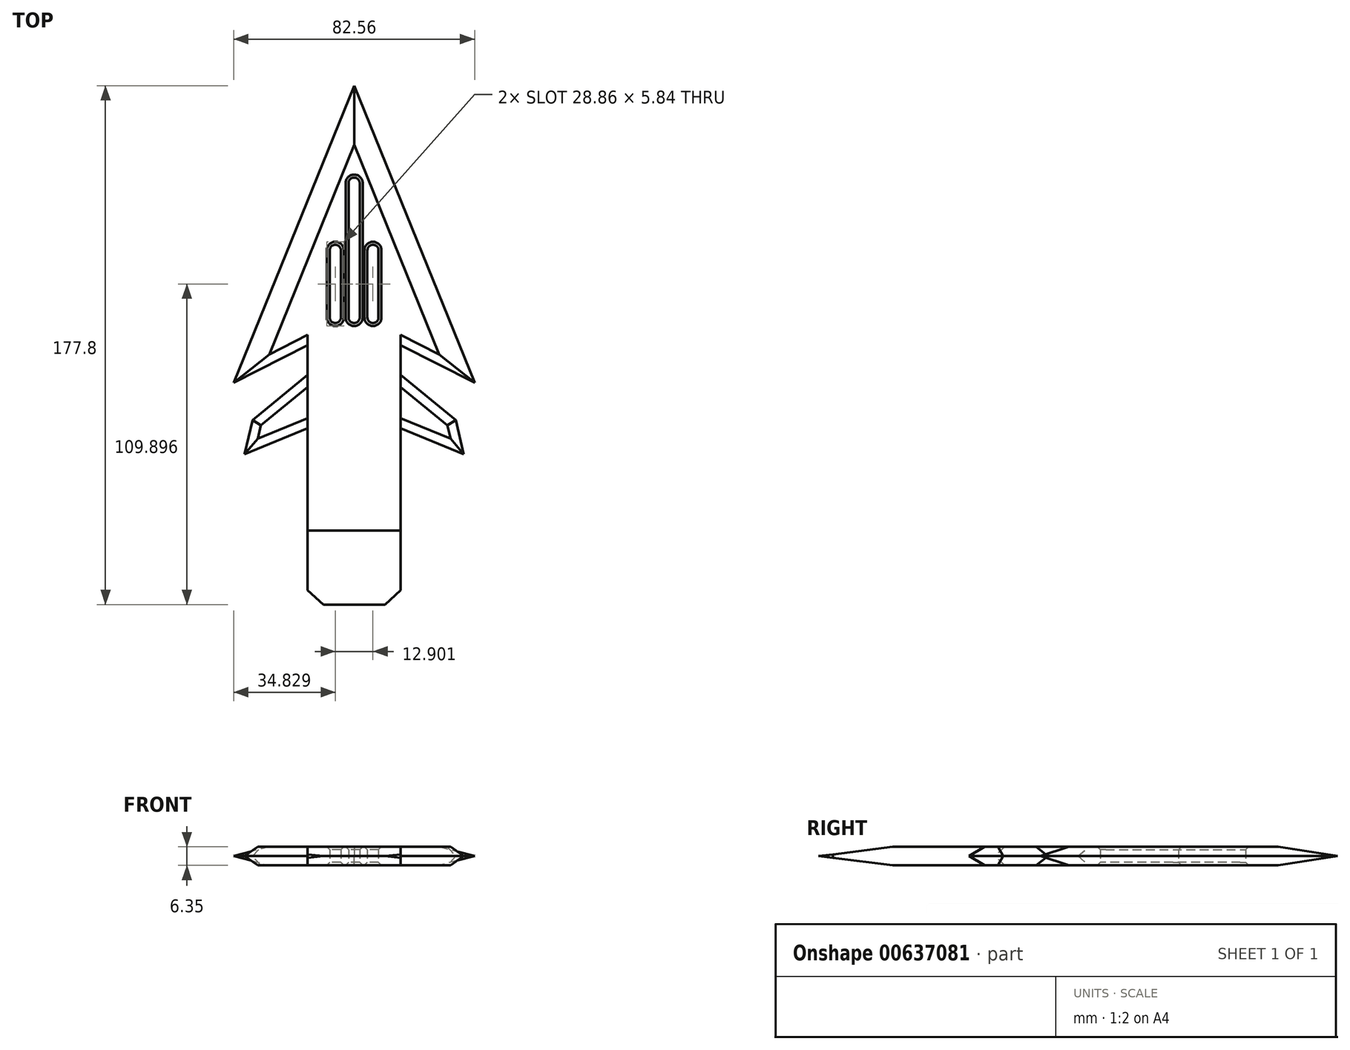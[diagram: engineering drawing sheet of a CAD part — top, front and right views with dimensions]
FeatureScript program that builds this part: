
annotation { "Feature Type Name" : "Feature", "Feature Type Description" : "" }
export const myFeature = defineFeature(function(context is Context, id is Id, definition is map)
    precondition{}
    {
        {
            var Q0;
            Q0=qCreatedBy(makeId("Top.planeOp"),FACE);
            var sketch = newSketch(context, id + "F0", { "sketchPlane" : qUnion([Q0])});
            skPoint(sketch, "E0.middle", {"position": v(0, 0) * mm});
            skLineSegment(sketch, "E1", {"start": v(0, 88.9) * mm, "end": v(41.28, -12.87) * mm});
            skLineSegment(sketch, "E2.MirrorCS", {"start": v(0, 88.9) * mm, "end": v(-41.28, -12.87) * mm});
            skLineSegment(sketch, "E3", {"start": v(15.9, -10.25) * mm, "end": v(34.78, -25.68) * mm});
            skLineSegment(sketch, "E4", {"start": v(34.78, -25.68) * mm, "end": v(37.57, -37.31) * mm});
            skLineSegment(sketch, "E5", {"start": v(37.57, -37.31) * mm, "end": v(15.9, -28.53) * mm});
            skLineSegment(sketch, "E6.MirrorCS", {"start": v(-15.9, -10.25) * mm, "end": v(-34.78, -25.68) * mm});
            skLineSegment(sketch, "E7.MirrorCS", {"start": v(-34.78, -25.68) * mm, "end": v(-37.57, -37.31) * mm});
            skLineSegment(sketch, "E8.MirrorCS", {"start": v(-37.57, -37.31) * mm, "end": v(-15.9, -28.53) * mm});
            skLineSegment(sketch, "E9", {"start": v(0, 55.53) * mm, "end": v(0, 9.49) * mm});
            skLineSegment(sketch, "E10", {"start": v(6.45, 32.5) * mm, "end": v(6.45, 9.49) * mm});
            skPoint(sketch, "E10.startSnap0", {"position": v(0, 32.5) * mm});
            skLineSegment(sketch, "E11.MirrorCS", {"start": v(-6.45, 32.5) * mm, "end": v(-6.45, 9.49) * mm});
            skArc(sketch, "E12.0.startCap", {"start": v(-1.9, 55.53) * mm, "mid": v(0, 57.43) * mm, "end": v(1.9, 55.53) * mm});
            skArc(sketch, "E12.0.endCap", {"start": v(1.9, 9.49) * mm, "mid": v(0, 7.58) * mm, "end": v(-1.9, 9.49) * mm});
            skLineSegment(sketch, "E12.0.left", {"start": v(1.9, 55.53) * mm, "end": v(1.9, 9.49) * mm});
            skLineSegment(sketch, "E12.0.right", {"start": v(-1.9, 55.53) * mm, "end": v(-1.9, 9.49) * mm});
            skArc(sketch, "E12.1.startCap", {"start": v(4.55, 32.5) * mm, "mid": v(6.45, 34.41) * mm, "end": v(8.36, 32.5) * mm});
            skArc(sketch, "E12.1.endCap", {"start": v(8.36, 9.49) * mm, "mid": v(6.45, 7.58) * mm, "end": v(4.55, 9.49) * mm});
            skLineSegment(sketch, "E12.1.left", {"start": v(8.36, 32.5) * mm, "end": v(8.36, 9.49) * mm});
            skLineSegment(sketch, "E12.1.right", {"start": v(4.55, 32.5) * mm, "end": v(4.55, 9.49) * mm});
            skArc(sketch, "E12.2.startCap", {"start": v(-8.36, 32.5) * mm, "mid": v(-6.45, 34.41) * mm, "end": v(-4.55, 32.5) * mm});
            skArc(sketch, "E12.2.endCap", {"start": v(-4.55, 9.49) * mm, "mid": v(-6.45, 7.58) * mm, "end": v(-8.36, 9.49) * mm});
            skLineSegment(sketch, "E12.2.left", {"start": v(-4.55, 32.5) * mm, "end": v(-4.55, 9.49) * mm});
            skLineSegment(sketch, "E12.2.right", {"start": v(-8.36, 32.5) * mm, "end": v(-8.36, 9.49) * mm});
            skLineSegment(sketch, "E13", {"start": v(-15.9, -83.97) * mm, "end": v(-10.53, -88.9) * mm});
            skLineSegment(sketch, "E14.MirrorCS", {"start": v(15.9, -83.97) * mm, "end": v(10.53, -88.9) * mm});
            skLineSegment(sketch, "E15", {"start": v(-15.9, 0) * mm, "end": v(-15.9, -83.97) * mm});
            skLineSegment(sketch, "E16.MirrorCS", {"start": v(15.9, 0) * mm, "end": v(15.9, -83.97) * mm});
            skLineSegment(sketch, "E17", {"start": v(-10.53, -88.9) * mm, "end": v(10.53, -88.9) * mm});
            skLineSegment(sketch, "E18", {"start": v(-15.9, 0) * mm, "end": v(-41.28, -12.87) * mm});
            skLineSegment(sketch, "E19", {"start": v(41.28, -12.87) * mm, "end": v(15.9, 0) * mm});
            skSolve(sketch);
        }
        {
            var Q0;
            Q0=makeQuery(id+"F0.imprint","IMPRINT",FACE,{"disambiguationData":[TD([[makeQuery(id+"F0.imprint","IMPRINT",EDGE,{"derivedFrom":sQuery(id+"F0.wireOp",EDGE,"E1")}),-1.0]])]});
            extrude(context, id + "F1", {"entities" : qUnion([Q0]), "depth" : 6.35 * mm, "offsetDistance" : 25.4 * mm});
        }
        {
            var Q0;
            {var subQ0=sQuery(id+"F0.wireOp",EDGE,"E6.MirrorCS");Q0=makeQuery(id+"F0.imprint","IMPRINT",FACE,{"disambiguationData":[TD([[makeQuery(id+"F0.imprint","IMPRINT",EDGE,{"derivedFrom":subQ0}),1.0]])]});}
            extrude(context, id + "F2", {"entities" : qUnion([Q0]), "depth" : 6.35 * mm, "offsetDistance" : 25.4 * mm});
        }
        {
            var Q0;
            {var subQ0=sQuery(id+"F0.wireOp",EDGE,"E3");Q0=makeQuery(id+"F0.imprint","IMPRINT",FACE,{"disambiguationData":[TD([[makeQuery(id+"F0.imprint","IMPRINT",EDGE,{"derivedFrom":subQ0}),-1.0]])]});}
            extrude(context, id + "F3", {"entities" : qUnion([Q0]), "depth" : 6.35 * mm, "offsetDistance" : 25.4 * mm});
        }
        {
            var Q0;
            Q0=makeQuery(id+"F1.opExtrude","CAP_EDGE",EDGE,{"disambiguationData":[OSD([sQuery(id+"F0.wireOp",EDGE,"E1")])],"isStart":false});
            var Q1;
            Q1=makeQuery(id+"F1.opExtrude","CAP_EDGE",EDGE,{"disambiguationData":[OSD([sQuery(id+"F0.wireOp",EDGE,"E2.MirrorCS")])],"isStart":false});
            var Q2;
            Q2=makeQuery(id+"F1.opExtrude","CAP_EDGE",EDGE,{"disambiguationData":[OSD([sQuery(id+"F0.wireOp",EDGE,"E2.MirrorCS")])],"isStart":true});
            var Q3;
            Q3=makeQuery(id+"F1.opExtrude","CAP_EDGE",EDGE,{"disambiguationData":[OSD([sQuery(id+"F0.wireOp",EDGE,"E1")])],"isStart":true});
            chamfer(context, id + "F4", {"entities" : qUnion([Q0, Q1, Q2, Q3]), "chamferType" : ChamferType.TWO_OFFSETS, "width1" : 3.17 * mm, "oppositeDirection" : false, "width2" : 7.62 * mm, "tangentPropagation" : true});
        }
        {
            var Q0;
            Q0=makeQuery(id+"F1.opExtrude","CAP_EDGE",EDGE,{"disambiguationData":[OSD([sQuery(id+"F0.wireOp",EDGE,"E19")])],"isStart":false});
            var Q1;
            Q1=makeQuery(id+"F1.opExtrude","CAP_EDGE",EDGE,{"disambiguationData":[OSD([sQuery(id+"F0.wireOp",EDGE,"E19")])],"isStart":true});
            var Q2;
            Q2=makeQuery(id+"F1.opExtrude","CAP_EDGE",EDGE,{"disambiguationData":[OSD([sQuery(id+"F0.wireOp",EDGE,"E18")])],"isStart":false});
            var Q3;
            Q3=makeQuery(id+"F1.opExtrude","CAP_EDGE",EDGE,{"disambiguationData":[OSD([sQuery(id+"F0.wireOp",EDGE,"E18")])],"isStart":true});
            chamfer(context, id + "F5", {"entities" : qUnion([Q0, Q1, Q2, Q3]), "chamferType" : ChamferType.TWO_OFFSETS, "width1" : 3.17 * mm, "oppositeDirection" : false, "width2" : 3.17 * mm, "tangentPropagation" : true});
        }
        {
            var Q0;
            Q0=makeQuery(id+"F2.opExtrude","CAP_EDGE",EDGE,{"disambiguationData":[OSD([sQuery(id+"F0.wireOp",EDGE,"E6.MirrorCS")])],"isStart":false});
            var Q1;
            Q1=makeQuery(id+"F2.opExtrude","CAP_EDGE",EDGE,{"disambiguationData":[OSD([sQuery(id+"F0.wireOp",EDGE,"E6.MirrorCS")])],"isStart":true});
            var Q2;
            Q2=makeQuery(id+"F2.opExtrude","CAP_EDGE",EDGE,{"disambiguationData":[OSD([sQuery(id+"F0.wireOp",EDGE,"E7.MirrorCS")])],"isStart":false});
            var Q3;
            Q3=makeQuery(id+"F2.opExtrude","CAP_EDGE",EDGE,{"disambiguationData":[OSD([sQuery(id+"F0.wireOp",EDGE,"E7.MirrorCS")])],"isStart":true});
            var Q4;
            Q4=makeQuery(id+"F2.opExtrude","CAP_EDGE",EDGE,{"disambiguationData":[OSD([sQuery(id+"F0.wireOp",EDGE,"E8.MirrorCS")])],"isStart":true});
            var Q5;
            Q5=makeQuery(id+"F2.opExtrude","CAP_EDGE",EDGE,{"disambiguationData":[OSD([sQuery(id+"F0.wireOp",EDGE,"E8.MirrorCS")])],"isStart":false});
            var Q6;
            Q6=makeQuery(id+"F3.opExtrude","CAP_EDGE",EDGE,{"disambiguationData":[OSD([sQuery(id+"F0.wireOp",EDGE,"E3")])],"isStart":false});
            var Q7;
            Q7=makeQuery(id+"F3.opExtrude","CAP_EDGE",EDGE,{"disambiguationData":[OSD([sQuery(id+"F0.wireOp",EDGE,"E3")])],"isStart":true});
            var Q8;
            Q8=makeQuery(id+"F3.opExtrude","CAP_EDGE",EDGE,{"disambiguationData":[OSD([sQuery(id+"F0.wireOp",EDGE,"E4")])],"isStart":true});
            var Q9;
            Q9=makeQuery(id+"F3.opExtrude","CAP_EDGE",EDGE,{"disambiguationData":[OSD([sQuery(id+"F0.wireOp",EDGE,"E4")])],"isStart":false});
            var Q10;
            Q10=makeQuery(id+"F3.opExtrude","CAP_EDGE",EDGE,{"disambiguationData":[OSD([sQuery(id+"F0.wireOp",EDGE,"E5")])],"isStart":false});
            var Q11;
            Q11=makeQuery(id+"F3.opExtrude","CAP_EDGE",EDGE,{"disambiguationData":[OSD([sQuery(id+"F0.wireOp",EDGE,"E5")])],"isStart":true});
            chamfer(context, id + "F6", {"entities" : qUnion([Q0, Q1, Q2, Q3, Q4, Q5, Q6, Q7, Q8, Q9, Q10, Q11]), "chamferType" : ChamferType.TWO_OFFSETS, "width1" : 3.17 * mm, "oppositeDirection" : false, "width2" : 3.17 * mm, "tangentPropagation" : true});
        }
        {
            var Q0;
            Q0=makeQuery(id+"F1.opExtrude","CAP_EDGE",EDGE,{"disambiguationData":[OSD([sQuery(id+"F0.wireOp",EDGE,"E12.2.right")])],"isStart":false});
            var Q1;
            Q1=makeQuery(id+"F1.opExtrude","CAP_EDGE",EDGE,{"disambiguationData":[OSD([sQuery(id+"F0.wireOp",EDGE,"E12.2.endCap")])],"isStart":false});
            var Q2;
            Q2=makeQuery(id+"F1.opExtrude","CAP_EDGE",EDGE,{"disambiguationData":[OSD([sQuery(id+"F0.wireOp",EDGE,"E12.2.left")])],"isStart":false});
            var Q3;
            Q3=makeQuery(id+"F1.opExtrude","CAP_EDGE",EDGE,{"disambiguationData":[OSD([sQuery(id+"F0.wireOp",EDGE,"E12.2.startCap")])],"isStart":false});
            var Q4;
            Q4=makeQuery(id+"F1.opExtrude","CAP_EDGE",EDGE,{"disambiguationData":[OSD([sQuery(id+"F0.wireOp",EDGE,"E12.0.right")])],"isStart":false});
            var Q5;
            Q5=makeQuery(id+"F1.opExtrude","CAP_EDGE",EDGE,{"disambiguationData":[OSD([sQuery(id+"F0.wireOp",EDGE,"E12.0.endCap")])],"isStart":false});
            var Q6;
            Q6=makeQuery(id+"F1.opExtrude","CAP_EDGE",EDGE,{"disambiguationData":[OSD([sQuery(id+"F0.wireOp",EDGE,"E12.0.left")])],"isStart":false});
            var Q7;
            Q7=makeQuery(id+"F1.opExtrude","CAP_EDGE",EDGE,{"disambiguationData":[OSD([sQuery(id+"F0.wireOp",EDGE,"E12.0.startCap")])],"isStart":false});
            var Q8;
            Q8=makeQuery(id+"F1.opExtrude","CAP_EDGE",EDGE,{"disambiguationData":[OSD([sQuery(id+"F0.wireOp",EDGE,"E12.1.left")])],"isStart":false});
            var Q9;
            Q9=makeQuery(id+"F1.opExtrude","CAP_EDGE",EDGE,{"disambiguationData":[OSD([sQuery(id+"F0.wireOp",EDGE,"E12.1.startCap")])],"isStart":false});
            var Q10;
            Q10=makeQuery(id+"F1.opExtrude","CAP_EDGE",EDGE,{"disambiguationData":[OSD([sQuery(id+"F0.wireOp",EDGE,"E12.1.right")])],"isStart":false});
            var Q11;
            Q11=makeQuery(id+"F1.opExtrude","CAP_EDGE",EDGE,{"disambiguationData":[OSD([sQuery(id+"F0.wireOp",EDGE,"E12.1.endCap")])],"isStart":false});
            var Q12;
            Q12=makeQuery(id+"F1.opExtrude","CAP_EDGE",EDGE,{"disambiguationData":[OSD([sQuery(id+"F0.wireOp",EDGE,"E12.2.endCap")])],"isStart":true});
            var Q13;
            Q13=makeQuery(id+"F1.opExtrude","CAP_EDGE",EDGE,{"disambiguationData":[OSD([sQuery(id+"F0.wireOp",EDGE,"E12.0.endCap")])],"isStart":true});
            var Q14;
            Q14=makeQuery(id+"F1.opExtrude","CAP_EDGE",EDGE,{"disambiguationData":[OSD([sQuery(id+"F0.wireOp",EDGE,"E12.1.endCap")])],"isStart":true});
            var Q15;
            Q15=makeQuery(id+"F1.opExtrude","CAP_EDGE",EDGE,{"disambiguationData":[OSD([sQuery(id+"F0.wireOp",EDGE,"E12.1.right")])],"isStart":true});
            var Q16;
            Q16=makeQuery(id+"F1.opExtrude","CAP_EDGE",EDGE,{"disambiguationData":[OSD([sQuery(id+"F0.wireOp",EDGE,"E12.1.left")])],"isStart":true});
            var Q17;
            Q17=makeQuery(id+"F1.opExtrude","CAP_EDGE",EDGE,{"disambiguationData":[OSD([sQuery(id+"F0.wireOp",EDGE,"E12.0.right")])],"isStart":true});
            var Q18;
            Q18=makeQuery(id+"F1.opExtrude","CAP_EDGE",EDGE,{"disambiguationData":[OSD([sQuery(id+"F0.wireOp",EDGE,"E12.0.left")])],"isStart":true});
            var Q19;
            Q19=makeQuery(id+"F1.opExtrude","CAP_EDGE",EDGE,{"disambiguationData":[OSD([sQuery(id+"F0.wireOp",EDGE,"E12.2.left")])],"isStart":true});
            var Q20;
            Q20=makeQuery(id+"F1.opExtrude","CAP_EDGE",EDGE,{"disambiguationData":[OSD([sQuery(id+"F0.wireOp",EDGE,"E12.2.right")])],"isStart":true});
            var Q21;
            Q21=makeQuery(id+"F1.opExtrude","CAP_EDGE",EDGE,{"disambiguationData":[OSD([sQuery(id+"F0.wireOp",EDGE,"E12.1.startCap")])],"isStart":true});
            var Q22;
            Q22=makeQuery(id+"F1.opExtrude","CAP_EDGE",EDGE,{"disambiguationData":[OSD([sQuery(id+"F0.wireOp",EDGE,"E12.2.startCap")])],"isStart":true});
            var Q23;
            Q23=makeQuery(id+"F1.opExtrude","CAP_EDGE",EDGE,{"disambiguationData":[OSD([sQuery(id+"F0.wireOp",EDGE,"E12.0.startCap")])],"isStart":true});
            chamfer(context, id + "F7", {"entities" : qUnion([Q0, Q1, Q2, Q3, Q4, Q5, Q6, Q7, Q8, Q9, Q10, Q11, Q12, Q13, Q14, Q15, Q16, Q17, Q18, Q19, Q20, Q21, Q22, Q23]), "width" : 1.02 * mm, "tangentPropagation" : true});
        }
        {
            var Q0;
            Q0=makeQuery(id+"F1.opExtrude","CAP_EDGE",EDGE,{"disambiguationData":[OSD([sQuery(id+"F0.wireOp",EDGE,"E17")])],"isStart":false});
            var Q1;
            Q1=makeQuery(id+"F1.opExtrude","CAP_EDGE",EDGE,{"disambiguationData":[OSD([sQuery(id+"F0.wireOp",EDGE,"E17")])],"isStart":true});
            chamfer(context, id + "F8", {"entities" : qUnion([Q0, Q1]), "chamferType" : ChamferType.TWO_OFFSETS, "width1" : 25.4 * mm, "oppositeDirection" : false, "width2" : 3.17 * mm, "tangentPropagation" : true});
        }
    });
